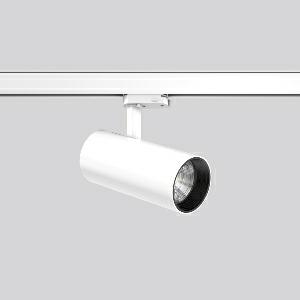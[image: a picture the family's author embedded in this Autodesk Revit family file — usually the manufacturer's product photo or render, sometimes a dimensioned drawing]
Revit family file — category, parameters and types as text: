
# Revit family: deecos_s_mini_742200_002_189c
name_source: partatom
category: Lighting Fixtures
units: mm (PartAtom-declared; Revit-internal decimal feet)

## family parameters
Cut with Voids When Loaded = No
Host = Face
Light Source = No
Part Type = Normal
Room Calculation Point = No
Round Connector Dimension = Use Diameter
Shared = No

## types (1)
- DEECOS S mini (1 x LED Modul 930, 2000 lm, 3000)
    Apparent Load = 20 VA
    Approval mark = CE
    CIE Flux Codes = 98 100 100 100 100
    Color Rendering = 90
    Color Temperature = 3000
    Default Elevation = 1800 mm
    Description = Series: DEECOS S mini
LED surface-mounted projector in modern design with no visible cooling ribs. Housing: die-cast aluminium, powder-coated. Rotation range: 356°. Swivel range: 90°. Black plastic ring and recessed LED to prevent glare from the side. Optical assembly with lens made of plastic (polycarbonate) for the best homogeneous light distribution - can be changed without tools. Best colour rendering index Ra>90. With multi adaptor for 3-circuit tracks 230 V. Suitable for Track on ceiling, Wall track. High quality converter without flickering and stroboscopic effect. The following accessories can be mounted without use of tools: interchangeable lenses, decorative glasses, honeycomb louvre, clear and frosted diffusers, white interchangeable plastic ring. 
Colour: traffic white, matt (RAL 9016)
Diameter: 87 mm
Height: 214 mm
Lamp: LED
Socket: without socket
Colour temperature: 3000K
Colour rendering index (CRI): 92
System power: 20 W
Rated luminous flux: 2000 lm
Luminous efficiency: 100 lm/W
Control gear: Regulated power supply
Protection class: I
Type of protection: IP 20
    Height = 214 mm
    Lamp = 1 x LED Modul 930
    Lamp Light Flux = 2000 lm
    Lamp count = 1
    Length = 87 mm
    Lifetime = 50000 h
    Luminous efficacy = 100 lm/W
    Manufacturer = RZB
    ModVariant = No
    Model = 742200.002
    Mounting Place = Ceiling
    Mounting Type = Rail mounted
    Number of Poles = 1
    OnlyDefault = Yes
    Power Factor = 1
    Product Name = DEECOS S mini
    Product group = Track mounted projectors
    ProductGroupID = 301
    Protection Class = Protection class I
    Protection Degree = IP 20
    RLX_Detail_Level = 1
    RLX_Emergency_Light_Flux = 0 lm
    RLX_Emergency_Type = 0
    RLX_Emergency_Type_DB = No
    RlxData = <blob elided: 35313 chars, md5=e639bf13>
    Socket = socket
    Standby Power = 0 W
    System Light Flux = 2000 lm
    System Power = 20 W
    Type Comments = Product without accessories
    Type Image = 741930.002.jpg
    URL = http://relux.com
    VarID = ---
    Voltage = 230 V
    Voltage Range = 220-240 V
    Weight = 0.00 kg
    Width = 0 mm  [stored 0 ft]

note: [stored X ft] marks values corroborated as IEEE doubles in the binary element streams (Revit-internal decimal feet)

## geometry (parser evidence)
native form markers: Blend x4, Sweep x14
no freeform markers — native parametric forms only
